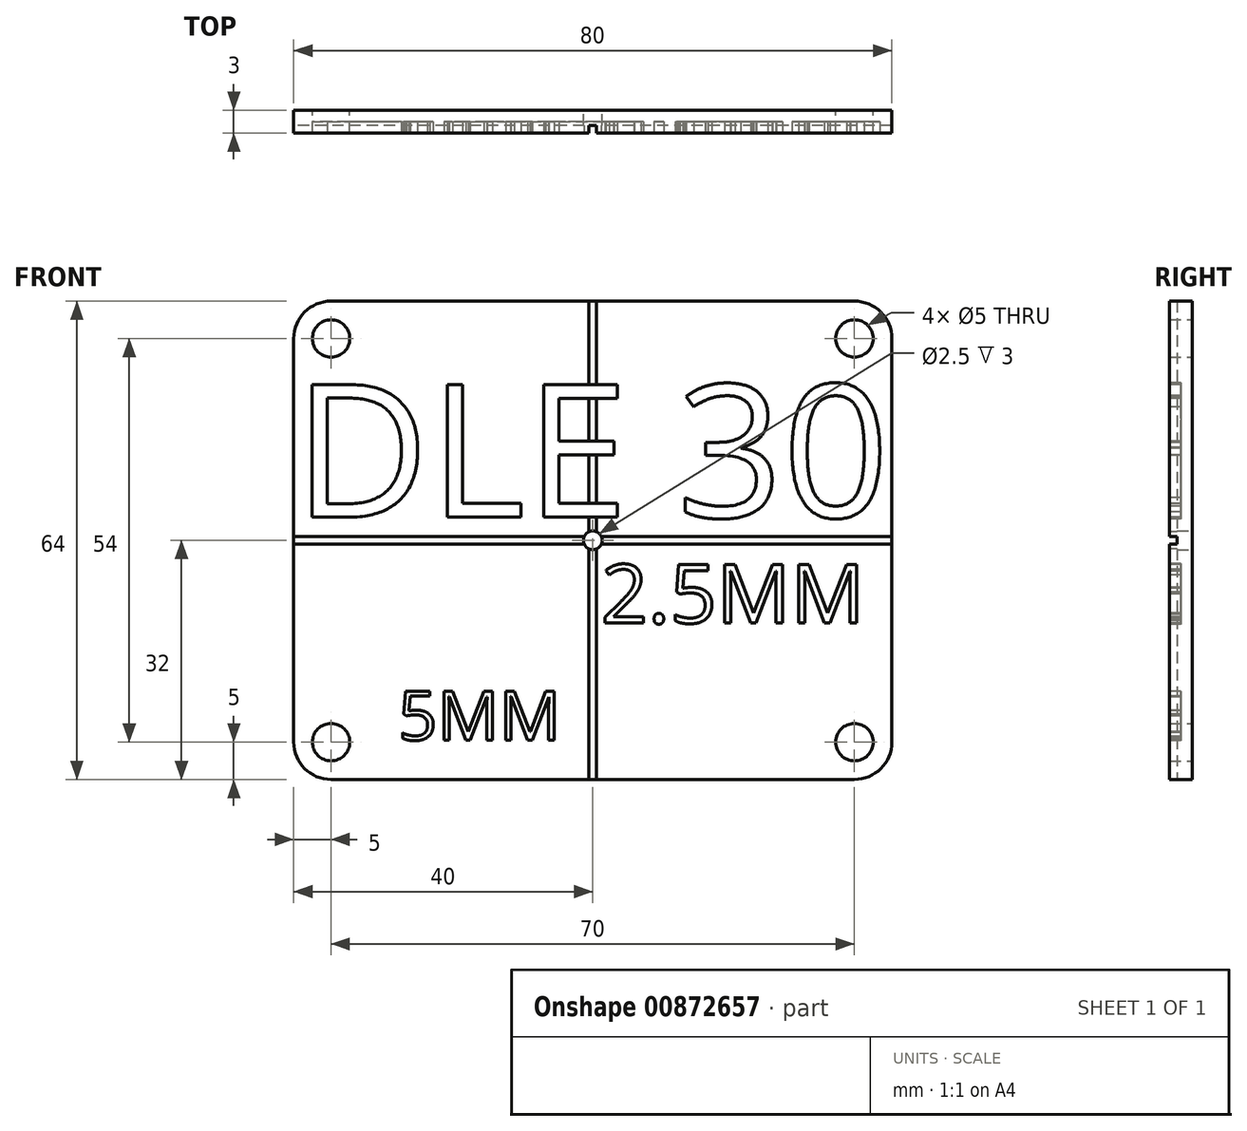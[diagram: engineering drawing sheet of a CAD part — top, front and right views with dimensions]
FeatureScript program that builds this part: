
annotation { "Feature Type Name" : "Feature", "Feature Type Description" : "" }
export const myFeature = defineFeature(function(context is Context, id is Id, definition is map)
    precondition{}
    {
        {
            var Q0;
            Q0=qCreatedBy(makeId("Front.planeOp"),FACE);
            var sketch = newSketch(context, id + "F0", { "sketchPlane" : qUnion([Q0])});
            skLineSegment(sketch, "E0.bottom", {"start": v(35, -27) * mm, "end": v(32.5, -27) * mm});
            skLineSegment(sketch, "E0.top", {"start": v(35, 27) * mm, "end": v(32.5, 27) * mm});
            skLineSegment(sketch, "E0.left", {"start": v(35, -27) * mm, "end": v(35, -24.5) * mm});
            skLineSegment(sketch, "E0.right", {"start": v(-35, -27) * mm, "end": v(-35, -24.5) * mm});
            skPoint(sketch, "E0.middle", {"position": v(0, 0) * mm});
            skCircle(sketch, "E1", {"center": v(-35, 27) * mm, "radius": 2.5 * mm});
            skCircle(sketch, "E2", {"center": v(35, 27) * mm, "radius": 2.5 * mm});
            skCircle(sketch, "E3", {"center": v(35, -27) * mm, "radius": 2.5 * mm});
            skCircle(sketch, "E4", {"center": v(-35, -27) * mm, "radius": 2.5 * mm});
            skLineSegment(sketch, "E5.bottom", {"start": v(-35, 32) * mm, "end": v(35, 32) * mm});
            skLineSegment(sketch, "E5.top", {"start": v(-35, -32) * mm, "end": v(35, -32) * mm});
            skLineSegment(sketch, "E5.left", {"start": v(-40, 27) * mm, "end": v(-40, -27) * mm});
            skLineSegment(sketch, "E5.right", {"start": v(40, 27) * mm, "end": v(40, -27) * mm});
            skLineSegment(sketch, "E6.trimOffspring", {"start": v(-35, 24.5) * mm, "end": v(-35, 27) * mm});
            skLineSegment(sketch, "E7.trimOffspring", {"start": v(-32.5, 27) * mm, "end": v(-35, 27) * mm});
            skLineSegment(sketch, "E8.trimOffspring", {"start": v(35, 24.5) * mm, "end": v(35, 27) * mm});
            skLineSegment(sketch, "E9.trimOffspring", {"start": v(-32.5, -27) * mm, "end": v(-35, -27) * mm});
            skPoint(sketch, "E10.visualSharp", {"position": v(-40, 32) * mm});
            skArc(sketch, "E10.filletArc", {"start": v(-35, 32) * mm, "mid": v(-38.54, 30.54) * mm, "end": v(-40, 27) * mm});
            skPoint(sketch, "E11.visualSharp", {"position": v(-40, -32) * mm});
            skArc(sketch, "E11.filletArc", {"start": v(-40, -27) * mm, "mid": v(-38.54, -30.54) * mm, "end": v(-35, -32) * mm});
            skPoint(sketch, "E12.visualSharp", {"position": v(40, 32) * mm});
            skArc(sketch, "E12.filletArc", {"start": v(40, 27) * mm, "mid": v(38.54, 30.54) * mm, "end": v(35, 32) * mm});
            skPoint(sketch, "E13.visualSharp", {"position": v(40, -32) * mm});
            skArc(sketch, "E13.filletArc", {"start": v(35, -32) * mm, "mid": v(38.54, -30.54) * mm, "end": v(40, -27) * mm});
            skCircle(sketch, "E14", {"center": v(0, 0) * mm, "radius": 1.25 * mm});
            skSolve(sketch);
        }
        {
            var Q0;
            Q0=makeQuery(id+"F0.imprint","IMPRINT",FACE,{"disambiguationData":[TD([[makeQuery(id+"F0.imprint","IMPRINT",EDGE,{"derivedFrom":sQuery(id+"F0.wireOp",EDGE,"E5.bottom")}),-1.0]])]});
            extrude(context, id + "F1", {"entities" : qUnion([Q0]), "depth" : 3 * mm, "offsetDistance" : 25 * mm});
        }
        {
            var Q0;
            Q0=makeQuery(id+"F1.opExtrude","CAP_FACE",FACE,{"disambiguationData":[OSD([sQuery(id+"F0.wireOp",EDGE,"E1"),sQuery(id+"F0.wireOp",EDGE,"E2"),sQuery(id+"F0.wireOp",EDGE,"E3"),sQuery(id+"F0.wireOp",EDGE,"E4"),sQuery(id+"F0.wireOp",EDGE,"E5.bottom"),sQuery(id+"F0.wireOp",EDGE,"E5.top"),sQuery(id+"F0.wireOp",EDGE,"E5.left"),sQuery(id+"F0.wireOp",EDGE,"E5.right"),sQuery(id+"F0.wireOp",EDGE,"E10.filletArc"),sQuery(id+"F0.wireOp",EDGE,"E11.filletArc"),sQuery(id+"F0.wireOp",EDGE,"E12.filletArc"),sQuery(id+"F0.wireOp",EDGE,"E13.filletArc"),sQuery(id+"F0.wireOp",EDGE,"E14")])],"isStart":false});
            var sketch = newSketch(context, id + "F2", { "sketchPlane" : qUnion([Q0])});
            skText(sketch, "E15", { "text": "DLE 30", "fontName": "OpenSans-Regular.ttf"});
            const initialGuessF2  = {"E15": [-0.04, 0.00309, 1, 0, 0.01787]};
            skSetInitialGuess(sketch, initialGuessF2);
            skSolve(sketch);
        }
        {
            var Q0;
            Q0 = qSketchRegion(id + "F2", true);
            extrude(context, id + "F3", {"entities" : qUnion([Q0]), "operationType" : NewBodyOperationType.REMOVE, "oppositeDirection" : true, "depth" : 1.5 * mm, "offsetDistance" : 25 * mm});
        }
        {
            var Q0;
            {var subQ0=sQuery(id+"F0.wireOp",EDGE,"E10.filletArc");var subQ1=sQuery(id+"F0.wireOp",EDGE,"E5.right");var subQ2=sQuery(id+"F0.wireOp",EDGE,"E5.left");var subQ3=sQuery(id+"F0.wireOp",EDGE,"E5.top");var subQ4=sQuery(id+"F0.wireOp",EDGE,"E5.bottom");var subQ5=sQuery(id+"F0.wireOp",EDGE,"E11.filletArc");var subQ6=sQuery(id+"F0.wireOp",EDGE,"E1");var subQ7=sQuery(id+"F0.wireOp",EDGE,"E4");var subQ8=sQuery(id+"F0.wireOp",EDGE,"E2");var subQ9=sQuery(id+"F0.wireOp",EDGE,"E3");var subQ10=sQuery(id+"F0.wireOp",EDGE,"E12.filletArc");var subQ11=sQuery(id+"F0.wireOp",EDGE,"E13.filletArc");var subQ12=sQuery(id+"F0.wireOp",EDGE,"E14");Q0=makeQuery(id+"F3.boolean.opBoolean","SPLIT",FACE,{"disambiguationData":[TD([makeQuery(id+"F1.opExtrude","SWEPT_FACE",FACE,{"disambiguationData":[OSD([subQ6])]})])],"derivedFrom":makeQuery(id+"F1.opExtrude","CAP_FACE",FACE,{"disambiguationData":[OSD([subQ6,subQ8,subQ9,subQ7,subQ4,subQ3,subQ2,subQ1,subQ0,subQ5,subQ10,subQ11,subQ12])],"isStart":false})});}
            var sketch = newSketch(context, id + "F4", { "sketchPlane" : qUnion([Q0])});
            skText(sketch, "E16", { "text": "5MM\n", "fontName": "OpenSans-Regular.ttf"});
            skText(sketch, "E17", { "text": "2.5MM", "fontName": "OpenSans-Regular.ttf"});
            const initialGuessF4  = {"E16": [-0.02604, -0.02672, 1, 0, 0.0066], "E17": [0.00112, -0.01107, 1, 0, 0.00789]};
            skSetInitialGuess(sketch, initialGuessF4);
            skSolve(sketch);
        }
        {
            var Q0;
            Q0 = qSketchRegion(id + "F4", true);
            extrude(context, id + "F5", {"entities" : qUnion([Q0]), "operationType" : NewBodyOperationType.REMOVE, "oppositeDirection" : true, "depth" : 1.5 * mm, "offsetDistance" : 25 * mm});
        }
        {
            var Q0;
            {var subQ0=sQuery(id+"F0.wireOp",EDGE,"E10.filletArc");var subQ1=sQuery(id+"F0.wireOp",EDGE,"E5.right");var subQ2=sQuery(id+"F0.wireOp",EDGE,"E5.left");var subQ3=sQuery(id+"F0.wireOp",EDGE,"E5.top");var subQ4=sQuery(id+"F0.wireOp",EDGE,"E5.bottom");var subQ5=sQuery(id+"F0.wireOp",EDGE,"E11.filletArc");var subQ6=sQuery(id+"F0.wireOp",EDGE,"E1");var subQ7=sQuery(id+"F0.wireOp",EDGE,"E4");var subQ8=sQuery(id+"F0.wireOp",EDGE,"E2");var subQ9=sQuery(id+"F0.wireOp",EDGE,"E3");var subQ10=sQuery(id+"F0.wireOp",EDGE,"E12.filletArc");var subQ11=sQuery(id+"F0.wireOp",EDGE,"E13.filletArc");var subQ12=sQuery(id+"F0.wireOp",EDGE,"E14");Q0=makeQuery(id+"F3.boolean.opBoolean","SPLIT",FACE,{"disambiguationData":[TD([makeQuery(id+"F1.opExtrude","SWEPT_FACE",FACE,{"disambiguationData":[OSD([subQ6])]})])],"derivedFrom":makeQuery(id+"F1.opExtrude","CAP_FACE",FACE,{"disambiguationData":[OSD([subQ6,subQ8,subQ9,subQ7,subQ4,subQ3,subQ2,subQ1,subQ0,subQ5,subQ10,subQ11,subQ12])],"isStart":false})});}
            var sketch = newSketch(context, id + "F6", { "sketchPlane" : qUnion([Q0])});
            skPoint(sketch, "E18.orphan", {"position": v(-40, 0) * mm});
            skPoint(sketch, "E19.end.orphan", {"position": v(0, -32) * mm});
            skPoint(sketch, "E19.start.orphan", {"position": v(0, 32) * mm});
            skLineSegment(sketch, "E20.bottom", {"start": v(0, 32) * mm, "end": v(-0.5, 32) * mm});
            skLineSegment(sketch, "E20.top", {"start": v(0, -32) * mm, "end": v(-0.5, -32) * mm});
            skLineSegment(sketch, "E20.left", {"start": v(0, 32) * mm, "end": v(0, -32) * mm});
            skLineSegment(sketch, "E20.right", {"start": v(-0.5, 32) * mm, "end": v(-0.5, -32) * mm});
            skLineSegment(sketch, "E21.bottom", {"start": v(0, 32) * mm, "end": v(0.5, 32) * mm});
            skLineSegment(sketch, "E21.top", {"start": v(0, -32) * mm, "end": v(0.5, -32) * mm});
            skLineSegment(sketch, "E21.right", {"start": v(0.5, 32) * mm, "end": v(0.5, -32) * mm});
            skLineSegment(sketch, "E22.bottom", {"start": v(-40, 0) * mm, "end": v(40, 0) * mm});
            skLineSegment(sketch, "E22.top", {"start": v(-40, -0.5) * mm, "end": v(40, -0.5) * mm});
            skLineSegment(sketch, "E22.left", {"start": v(-40, 0) * mm, "end": v(-40, -0.5) * mm});
            skLineSegment(sketch, "E22.right", {"start": v(40, 0) * mm, "end": v(40, -0.5) * mm});
            skLineSegment(sketch, "E23.bottom", {"start": v(40, 0.5) * mm, "end": v(-40, 0.5) * mm});
            skLineSegment(sketch, "E23.top", {"start": v(40, 0) * mm, "end": v(-40, 0) * mm});
            skLineSegment(sketch, "E23.left", {"start": v(40, 0.5) * mm, "end": v(40, 0) * mm});
            skLineSegment(sketch, "E23.right", {"start": v(-40, 0.5) * mm, "end": v(-40, 0) * mm});
            skSolve(sketch);
        }
        {
            var Q0;
            {var subQ0=sQuery(id+"F6.wireOp",EDGE,"E22.left");Q0=makeQuery(id+"F6.imprint","IMPRINT",FACE,{"disambiguationData":[TD([[makeQuery(id+"F6.imprint","IMPRINT",EDGE,{"derivedFrom":subQ0}),1.0]])]});}
            var Q1;
            {var subQ0=sQuery(id+"F6.wireOp",EDGE,"E23.right");Q1=makeQuery(id+"F6.imprint","IMPRINT",FACE,{"disambiguationData":[TD([[makeQuery(id+"F6.imprint","IMPRINT",EDGE,{"derivedFrom":subQ0}),1.0]])]});}
            var Q2;
            {var subQ0=sQuery(id+"F6.wireOp",EDGE,"E20.top");Q2=makeQuery(id+"F6.imprint","IMPRINT",FACE,{"disambiguationData":[TD([[makeQuery(id+"F6.imprint","IMPRINT",EDGE,{"derivedFrom":subQ0}),1.0]])]});}
            var Q3;
            {var subQ0=sQuery(id+"F6.wireOp",EDGE,"E21.top");Q3=makeQuery(id+"F6.imprint","IMPRINT",FACE,{"disambiguationData":[TD([[makeQuery(id+"F6.imprint","IMPRINT",EDGE,{"derivedFrom":subQ0}),1.0]])]});}
            var Q4;
            {var subQ0=sQuery(id+"F6.wireOp",EDGE,"E22.right");Q4=makeQuery(id+"F6.imprint","IMPRINT",FACE,{"disambiguationData":[TD([[makeQuery(id+"F6.imprint","IMPRINT",EDGE,{"derivedFrom":subQ0}),-1.0]])]});}
            var Q5;
            {var subQ0=sQuery(id+"F6.wireOp",EDGE,"E23.left");Q5=makeQuery(id+"F6.imprint","IMPRINT",FACE,{"disambiguationData":[TD([[makeQuery(id+"F6.imprint","IMPRINT",EDGE,{"derivedFrom":subQ0}),-1.0]])]});}
            var Q6;
            {var subQ0=sQuery(id+"F6.wireOp",EDGE,"E20.right");var subQ1=makeQuery(id+"F3.boolean.opBoolean","COPY",EDGE,{"derivedFrom":makeQuery(id+"F3.opExtrude","CAP_EDGE",EDGE,{"disambiguationData":[OSD([sQuery(id+"F2.wireOp",EDGE,"E15.sketch_text.stroke-20")])],"isStart":true})});var subQ2=makeQuery(id+"F6.imprint","INTERSECT",VERTEX,{"derivedFrom":[subQ1,subQ0]});Q6=makeQuery(id+"F6.imprint","IMPRINT",FACE,{"disambiguationData":[TD([[makeQuery(id+"F6.imprint","IMPRINT",EDGE,{"disambiguationData":[TD([[subQ2,-1.0]])],"derivedFrom":subQ0}),1.0]])]});}
            var Q7;
            {var subQ0=sQuery(id+"F6.wireOp",EDGE,"E20.left");var subQ1=makeQuery(id+"F3.boolean.opBoolean","COPY",EDGE,{"derivedFrom":makeQuery(id+"F3.opExtrude","CAP_EDGE",EDGE,{"disambiguationData":[OSD([sQuery(id+"F2.wireOp",EDGE,"E15.sketch_text.stroke-20")])],"isStart":true})});var subQ2=makeQuery(id+"F6.imprint","INTERSECT",VERTEX,{"derivedFrom":[subQ1,subQ0]});Q7=makeQuery(id+"F6.imprint","IMPRINT",FACE,{"disambiguationData":[TD([[makeQuery(id+"F6.imprint","IMPRINT",EDGE,{"disambiguationData":[TD([[subQ2,-1.0]])],"derivedFrom":subQ0}),1.0]])]});}
            var Q8;
            {var subQ0=sQuery(id+"F6.wireOp",EDGE,"E20.right");var subQ1=makeQuery(id+"F3.boolean.opBoolean","COPY",EDGE,{"derivedFrom":makeQuery(id+"F3.opExtrude","CAP_EDGE",EDGE,{"disambiguationData":[OSD([sQuery(id+"F2.wireOp",EDGE,"E15.sketch_text.stroke-28")])],"isStart":true})});var subQ2=makeQuery(id+"F6.imprint","INTERSECT",VERTEX,{"derivedFrom":[subQ1,subQ0]});Q8=makeQuery(id+"F6.imprint","IMPRINT",FACE,{"disambiguationData":[TD([[makeQuery(id+"F6.imprint","IMPRINT",EDGE,{"disambiguationData":[TD([[subQ2,-1.0]])],"derivedFrom":subQ0}),1.0]])]});}
            var Q9;
            {var subQ0=sQuery(id+"F6.wireOp",EDGE,"E20.left");var subQ1=makeQuery(id+"F3.boolean.opBoolean","COPY",EDGE,{"derivedFrom":makeQuery(id+"F3.opExtrude","CAP_EDGE",EDGE,{"disambiguationData":[OSD([sQuery(id+"F2.wireOp",EDGE,"E15.sketch_text.stroke-28")])],"isStart":true})});var subQ2=makeQuery(id+"F6.imprint","INTERSECT",VERTEX,{"derivedFrom":[subQ1,subQ0]});Q9=makeQuery(id+"F6.imprint","IMPRINT",FACE,{"disambiguationData":[TD([[makeQuery(id+"F6.imprint","IMPRINT",EDGE,{"disambiguationData":[TD([[subQ2,-1.0]])],"derivedFrom":subQ0}),1.0]])]});}
            var Q10;
            {var subQ0=sQuery(id+"F6.wireOp",EDGE,"E20.right");var subQ1=makeQuery(id+"F3.boolean.opBoolean","COPY",EDGE,{"derivedFrom":makeQuery(id+"F3.opExtrude","CAP_EDGE",EDGE,{"disambiguationData":[OSD([sQuery(id+"F2.wireOp",EDGE,"E15.sketch_text.stroke-24")])],"isStart":true})});var subQ2=makeQuery(id+"F6.imprint","INTERSECT",VERTEX,{"derivedFrom":[subQ1,subQ0]});Q10=makeQuery(id+"F6.imprint","IMPRINT",FACE,{"disambiguationData":[TD([[makeQuery(id+"F6.imprint","IMPRINT",EDGE,{"disambiguationData":[TD([[subQ2,-1.0]])],"derivedFrom":subQ0}),1.0]])]});}
            var Q11;
            {var subQ0=sQuery(id+"F6.wireOp",EDGE,"E20.left");var subQ1=makeQuery(id+"F3.boolean.opBoolean","COPY",EDGE,{"derivedFrom":makeQuery(id+"F3.opExtrude","CAP_EDGE",EDGE,{"disambiguationData":[OSD([sQuery(id+"F2.wireOp",EDGE,"E15.sketch_text.stroke-24")])],"isStart":true})});var subQ2=makeQuery(id+"F6.imprint","INTERSECT",VERTEX,{"derivedFrom":[subQ1,subQ0]});Q11=makeQuery(id+"F6.imprint","IMPRINT",FACE,{"disambiguationData":[TD([[makeQuery(id+"F6.imprint","IMPRINT",EDGE,{"disambiguationData":[TD([[subQ2,-1.0]])],"derivedFrom":subQ0}),1.0]])]});}
            var Q12;
            {var subQ0=sQuery(id+"F6.wireOp",EDGE,"E20.bottom");Q12=makeQuery(id+"F6.imprint","IMPRINT",FACE,{"disambiguationData":[TD([[makeQuery(id+"F6.imprint","IMPRINT",EDGE,{"derivedFrom":subQ0}),-1.0]])]});}
            var Q13;
            {var subQ0=sQuery(id+"F6.wireOp",EDGE,"E21.bottom");Q13=makeQuery(id+"F6.imprint","IMPRINT",FACE,{"disambiguationData":[TD([[makeQuery(id+"F6.imprint","IMPRINT",EDGE,{"derivedFrom":subQ0}),-1.0]])]});}
            extrude(context, id + "F7", {"entities" : qUnion([Q0, Q1, Q2, Q3, Q4, Q5, Q6, Q7, Q8, Q9, Q10, Q11, Q12, Q13]), "operationType" : NewBodyOperationType.REMOVE, "oppositeDirection" : true, "depth" : 1 * mm, "offsetDistance" : 25 * mm});
        }
    });
